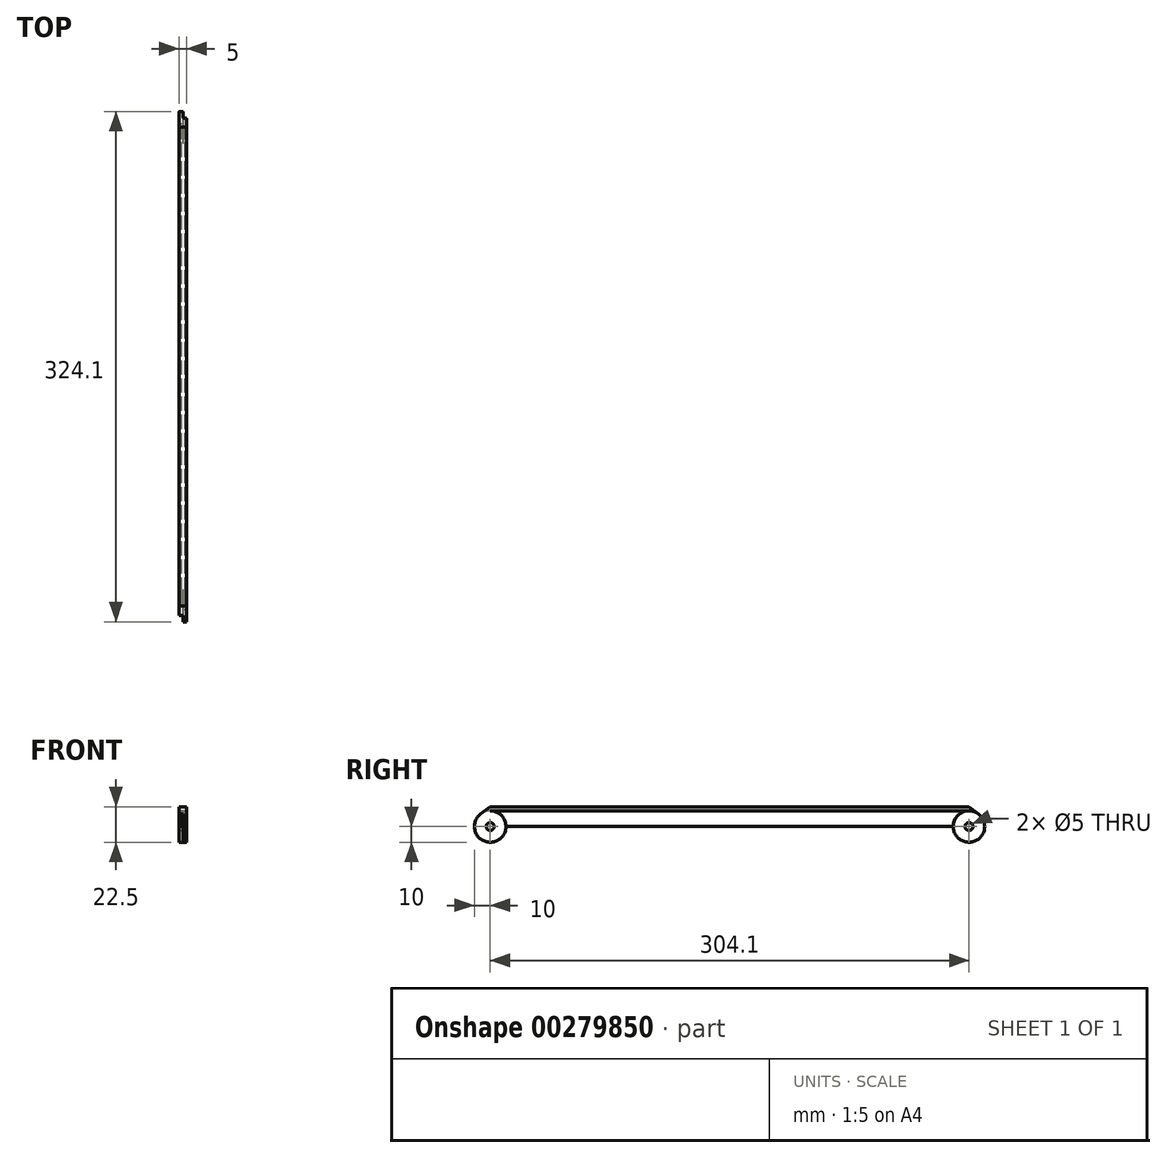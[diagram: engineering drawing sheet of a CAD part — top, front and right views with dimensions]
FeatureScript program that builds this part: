
annotation { "Feature Type Name" : "Feature", "Feature Type Description" : "" }
export const myFeature = defineFeature(function(context is Context, id is Id, definition is map)
    precondition{}
    {
        {
            var Q0;
            Q0=qCreatedBy(makeId("Right.planeOp"),FACE);
            var sketch = newSketch(context, id + "F0", { "sketchPlane" : qUnion([Q0])});
            skCircle(sketch, "E0", {"center": v(152.05, -12.5) * mm, "radius": 10 * mm});
            skCircle(sketch, "E1", {"center": v(-152.05, -12.5) * mm, "radius": 10 * mm});
            skCircle(sketch, "E2", {"center": v(152.05, -12.5) * mm, "radius": 2.5 * mm});
            skCircle(sketch, "E3", {"center": v(-152.05, -12.5) * mm, "radius": 2.5 * mm});
            skLineSegment(sketch, "E4", {"start": v(152.05, -2.5) * mm, "end": v(-152.05, -2.5) * mm});
            skLineSegment(sketch, "E5", {"start": v(152.05, 0) * mm, "end": v(-152.05, 0) * mm});
            skLineSegment(sketch, "E6", {"start": v(142.05, -12.5) * mm, "end": v(-142.05, -12.5) * mm});
            skLineSegment(sketch, "E7", {"start": v(152.05, 0) * mm, "end": v(158.05, -4.5) * mm});
            skLineSegment(sketch, "E8", {"start": v(-152.05, 0) * mm, "end": v(-158.05, -4.5) * mm});
            skLineSegment(sketch, "E9", {"start": v(152.05, -12.5) * mm, "end": v(142.05, -12.5) * mm, "construction": true});
            skLineSegment(sketch, "E10", {"start": v(-142.05, -12.5) * mm, "end": v(-152.05, -12.5) * mm, "construction": true});
            skLineSegment(sketch, "E11", {"start": v(152.05, -12.5) * mm, "end": v(152.05, -2.5) * mm, "construction": true});
            skLineSegment(sketch, "E12", {"start": v(-152.05, -12.5) * mm, "end": v(-152.05, -2.5) * mm, "construction": true});
            skLineSegment(sketch, "E13", {"start": v(152.05, -2.5) * mm, "end": v(152.05, 0) * mm, "construction": true});
            skLineSegment(sketch, "E14", {"start": v(-152.05, -2.5) * mm, "end": v(-152.05, 0) * mm, "construction": true});
            skSolve(sketch);
        }
        {
            var Q0;
            {var subQ0=sQuery(id+"F0.wireOp",EDGE,"E4");Q0=makeQuery(id+"F0.imprint","IMPRINT",FACE,{"disambiguationData":[TD([[makeQuery(id+"F0.imprint","IMPRINT",EDGE,{"derivedFrom":subQ0}),-1.0]])]});}
            extrude(context, id + "F1", {"entities" : qUnion([Q0]), "endBound" : BoundingType.SYMMETRIC, "depth" : 5 * mm});
        }
        {
            var Q0;
            {var subQ0=sQuery(id+"F0.wireOp",EDGE,"E4");Q0=makeQuery(id+"F0.imprint","IMPRINT",FACE,{"disambiguationData":[TD([[makeQuery(id+"F0.imprint","IMPRINT",EDGE,{"derivedFrom":subQ0}),1.0]])]});}
            extrude(context, id + "F2", {"entities" : qUnion([Q0]), "endBound" : BoundingType.SYMMETRIC, "depth" : 2.5 * mm});
        }
        {
            var Q0;
            Q0=makeQuery(id+"F0.imprint","IMPRINT",FACE,{"disambiguationData":[TD([[makeQuery(id+"F0.imprint","IMPRINT",EDGE,{"derivedFrom":sQuery(id+"F0.wireOp",EDGE,"E3")}),-1.0]])]});
            extrude(context, id + "F3", {"entities" : qUnion([Q0]), "operationType" : NewBodyOperationType.ADD, "depth" : 2.5 * mm});
        }
        {
            var Q0;
            Q0=makeQuery(id+"F0.imprint","IMPRINT",FACE,{"disambiguationData":[TD([[makeQuery(id+"F0.imprint","IMPRINT",EDGE,{"derivedFrom":sQuery(id+"F0.wireOp",EDGE,"E2")}),-1.0]])]});
            extrude(context, id + "F4", {"entities" : qUnion([Q0]), "operationType" : NewBodyOperationType.ADD, "oppositeDirection" : true, "depth" : 2.5 * mm});
        }
    });
